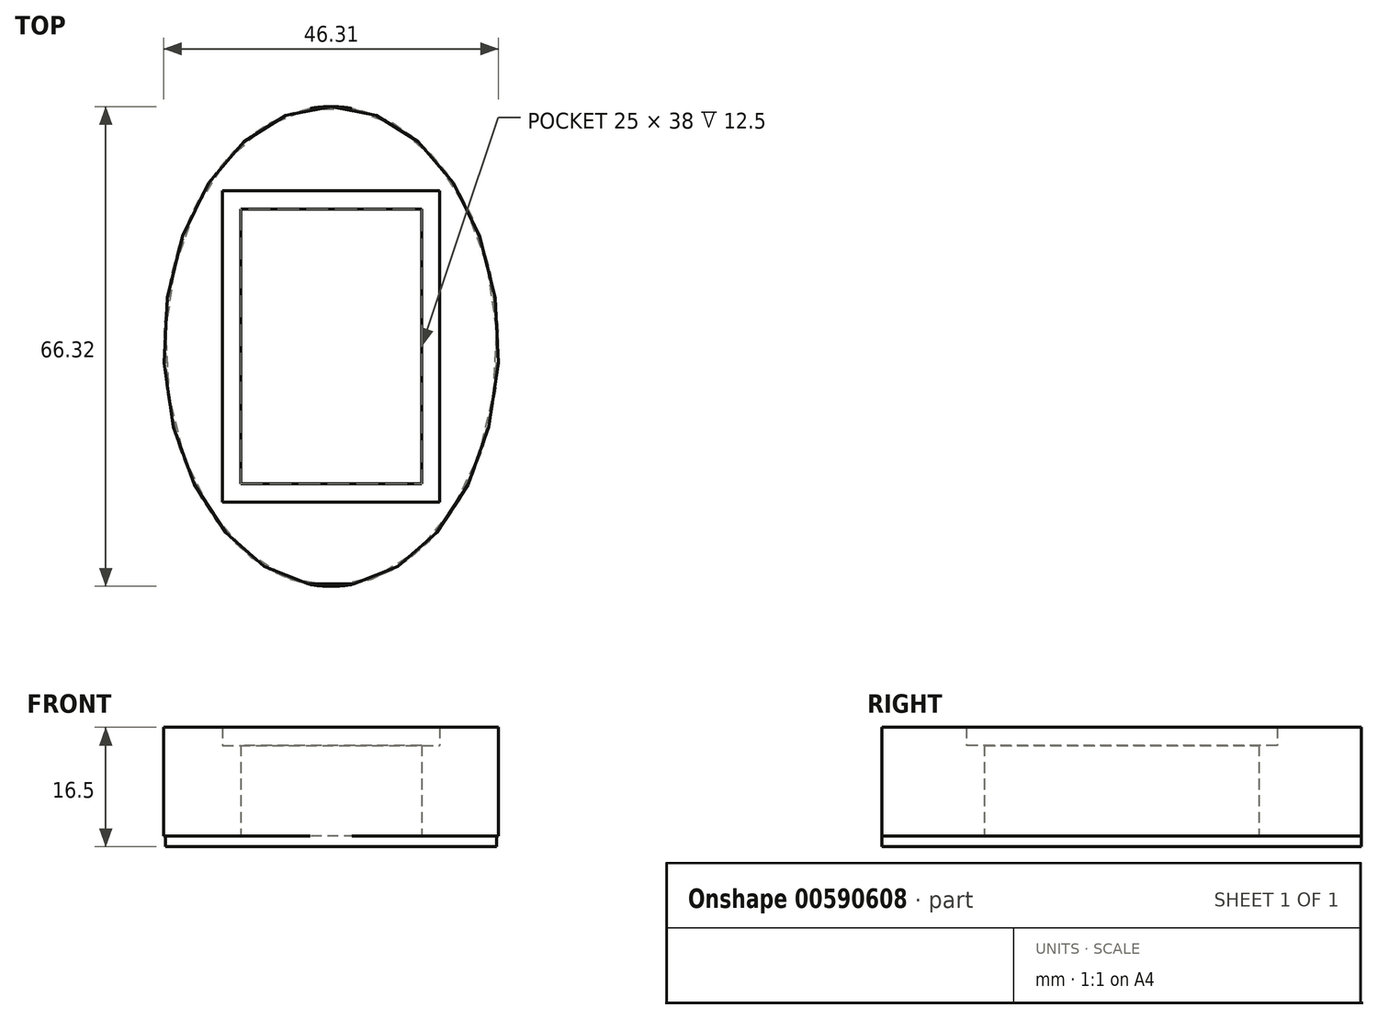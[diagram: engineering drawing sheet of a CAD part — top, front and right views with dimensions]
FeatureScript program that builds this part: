
annotation { "Feature Type Name" : "Feature", "Feature Type Description" : "" }
export const myFeature = defineFeature(function(context is Context, id is Id, definition is map)
    precondition{}
    {
        {
            var Q0;
            Q0=qCreatedBy(makeId("Top.planeOp"),FACE);
            var sketch = newSketch(context, id + "F0", { "sketchPlane" : qUnion([Q0])});
            skLineSegment(sketch, "E0.bottom", {"start": v(-34.2, 21.5) * mm, "end": v(-4.2, 21.5) * mm});
            skLineSegment(sketch, "E0.top", {"start": v(-34.2, -21.5) * mm, "end": v(-4.2, -21.5) * mm});
            skLineSegment(sketch, "E0.left", {"start": v(-34.2, 21.5) * mm, "end": v(-34.2, -21.5) * mm});
            skLineSegment(sketch, "E0.right", {"start": v(-4.2, 21.5) * mm, "end": v(-4.2, -21.5) * mm});
            skEllipse(sketch, "E1", {"center": v(-19.2, 0) * mm, "majorRadius": 33.16 * mm, "minorRadius": 23.16 * mm, "majorAxis": v(0, 1)});
            skSolve(sketch);
        }
        {
            var Q0;
            Q0=makeQuery(id+"F0.imprint","IMPRINT",FACE,{"disambiguationData":[TD([[makeQuery(id+"F0.imprint","IMPRINT",EDGE,{"derivedFrom":sQuery(id+"F0.wireOp",EDGE,"E0.bottom")}),1.0]])]});
            extrude(context, id + "F1", {"entities" : qUnion([Q0]), "depth" : 15 * mm, "offsetDistance" : 25 * mm});
        }
        {
            var Q0;
            Q0=makeQuery(id+"F1.opExtrude","CAP_FACE",FACE,{"disambiguationData":[OSD([sQuery(id+"F0.wireOp",EDGE,"E0.bottom"),sQuery(id+"F0.wireOp",EDGE,"E0.top"),sQuery(id+"F0.wireOp",EDGE,"E0.left"),sQuery(id+"F0.wireOp",EDGE,"E0.right"),sQuery(id+"F0.wireOp",EDGE,"E1")])],"isStart":true});
            var sketch = newSketch(context, id + "F2", { "sketchPlane" : qUnion([Q0])});
            skEllipse(sketch, "E2", {"center": v(-19.2, 0) * mm, "majorRadius": 33.16 * mm, "minorRadius": 22.88 * mm, "majorAxis": v(0, 1)});
            skSolve(sketch);
        }
        {
            var Q0;
            Q0 = qSketchRegion(id + "F2", true);
            extrude(context, id + "F3", {"entities" : qUnion([Q0]), "operationType" : NewBodyOperationType.ADD, "depth" : 1.5 * mm, "offsetDistance" : 25 * mm});
        }
        {
            var Q0;
            Q0=makeQuery(id+"F3.opExtrude","CAP_FACE",FACE,{"disambiguationData":[OSD([sQuery(id+"F2.wireOp",EDGE,"E2")])],"isStart":true});
            var sketch = newSketch(context, id + "F4", { "sketchPlane" : qUnion([Q0])});
            skLineSegment(sketch, "E3.bottom", {"start": v(-4.2, -21.5) * mm, "end": v(-34.2, -21.5) * mm});
            skLineSegment(sketch, "E3.top", {"start": v(-4.2, 21.5) * mm, "end": v(-34.2, 21.5) * mm});
            skLineSegment(sketch, "E3.left", {"start": v(-4.2, -21.5) * mm, "end": v(-4.2, 21.5) * mm});
            skLineSegment(sketch, "E3.right", {"start": v(-34.2, -21.5) * mm, "end": v(-34.2, 21.5) * mm});
            skLineSegment(sketch, "E4.bottom", {"start": v(-6.7, -19) * mm, "end": v(-31.7, -19) * mm});
            skLineSegment(sketch, "E4.top", {"start": v(-6.7, 19) * mm, "end": v(-31.7, 19) * mm});
            skLineSegment(sketch, "E4.left", {"start": v(-6.7, -19) * mm, "end": v(-6.7, 19) * mm});
            skLineSegment(sketch, "E4.right", {"start": v(-31.7, -19) * mm, "end": v(-31.7, 19) * mm});
            skSolve(sketch);
        }
        {
            var Q0;
            Q0 = qSketchRegion(id + "F4", true);
            extrude(context, id + "F5", {"entities" : qUnion([Q0]), "operationType" : NewBodyOperationType.ADD, "depth" : 12.5 * mm, "offsetDistance" : 25 * mm});
        }
    });
